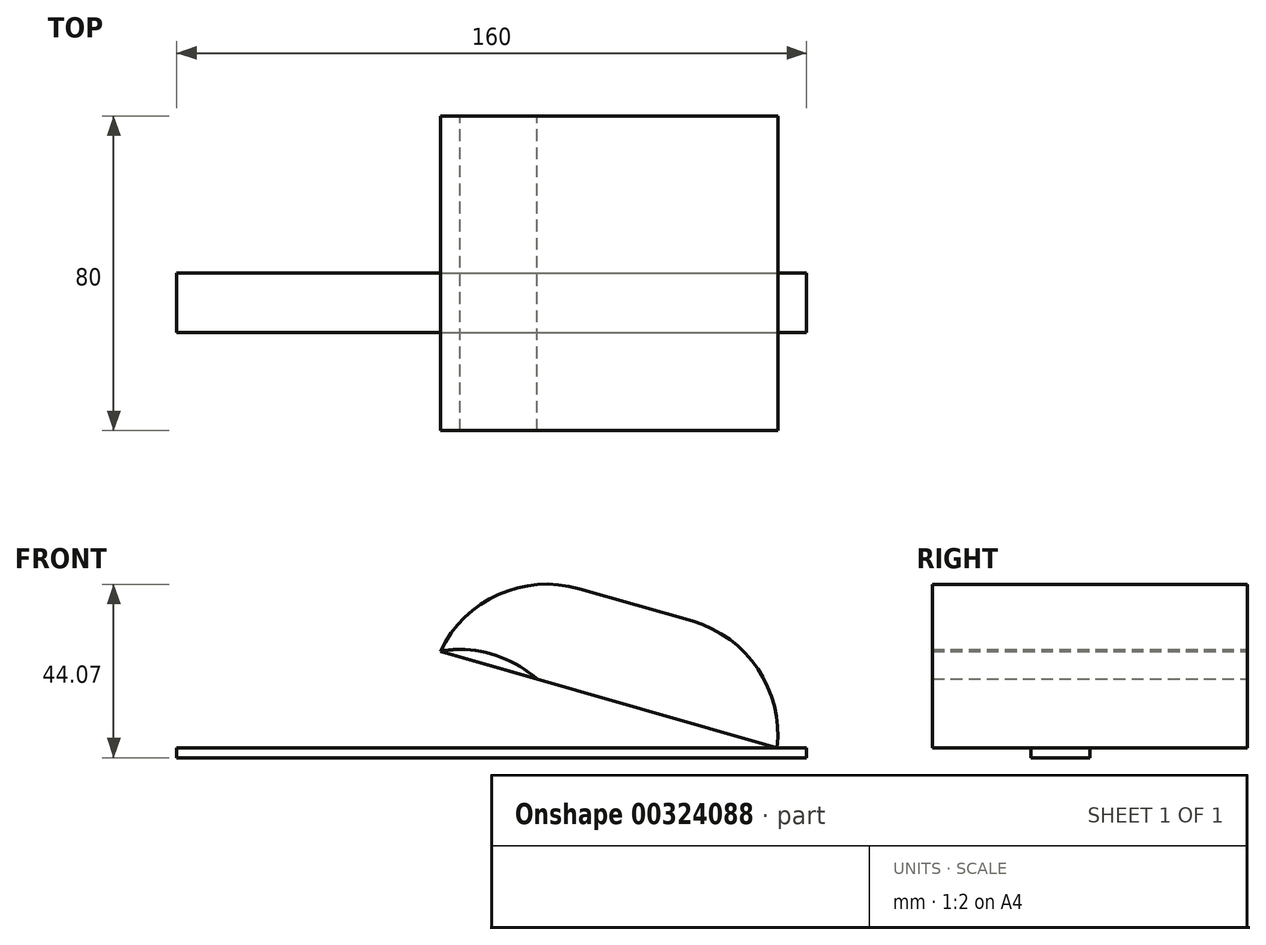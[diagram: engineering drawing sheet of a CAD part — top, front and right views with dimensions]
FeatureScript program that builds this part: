
annotation { "Feature Type Name" : "Feature", "Feature Type Description" : "" }
export const myFeature = defineFeature(function(context is Context, id is Id, definition is map)
    precondition{}
    {
        {
            var Q0;
            Q0=qCreatedBy(makeId("Front.planeOp"),FACE);
            var sketch = newSketch(context, id + "F0", { "sketchPlane" : qUnion([Q0])});
            skLineSegment(sketch, "E0.bottom", {"start": v(-80, 0) * mm, "end": v(80, 0) * mm});
            skLineSegment(sketch, "E0.top", {"start": v(-80, 2.5) * mm, "end": v(80, 2.5) * mm});
            skLineSegment(sketch, "E0.right", {"start": v(80, 0) * mm, "end": v(80, 2.5) * mm});
            skLineSegment(sketch, "E1", {"start": v(77.5, 0) * mm, "end": v(77.5, 2.5) * mm});
            skLineSegment(sketch, "E2", {"start": v(-77.5, 27.5) * mm, "end": v(11.5, 27.5) * mm});
            skLineSegment(sketch, "E3", {"start": v(11.5, 27.5) * mm, "end": v(11.5, 2.5) * mm});
            skLineSegment(sketch, "E4", {"start": v(11.5, 2.5) * mm, "end": v(-77.5, 2.5) * mm});
            skLineSegment(sketch, "E5", {"start": v(-6.16, 51.06) * mm, "end": v(79.4, 26.53) * mm});
            skLineSegment(sketch, "E6", {"start": v(79.4, 26.53) * mm, "end": v(72.5, 2.5) * mm});
            skLineSegment(sketch, "E7", {"start": v(72.5, 2.5) * mm, "end": v(-13.05, 27.03) * mm});
            skLineSegment(sketch, "E8", {"start": v(-13.05, 27.03) * mm, "end": v(-6.16, 51.06) * mm});
            skLineSegment(sketch, "E9", {"start": v(-77.5, 27.5) * mm, "end": v(-77.5, 2.5) * mm});
            skLineSegment(sketch, "E10", {"start": v(-80, 2.5) * mm, "end": v(-80, 0) * mm});
            skLineSegment(sketch, "E11.bottom", {"start": v(-80, 2.5) * mm, "end": v(-77.5, 2.5) * mm});
            skLineSegment(sketch, "E11.top", {"start": v(-80, 17.5) * mm, "end": v(-77.5, 17.5) * mm});
            skLineSegment(sketch, "E11.left", {"start": v(-80, 2.5) * mm, "end": v(-80, 17.5) * mm});
            skLineSegment(sketch, "E11.right", {"start": v(-77.5, 2.5) * mm, "end": v(-77.5, 17.5) * mm});
            skLineSegment(sketch, "E12.bottom", {"start": v(77.5, 2.5) * mm, "end": v(80, 2.5) * mm});
            skLineSegment(sketch, "E12.top", {"start": v(77.5, 17.5) * mm, "end": v(80, 17.5) * mm});
            skLineSegment(sketch, "E12.left", {"start": v(77.5, 2.5) * mm, "end": v(77.5, 17.5) * mm});
            skLineSegment(sketch, "E12.right", {"start": v(80, 2.5) * mm, "end": v(80, 17.5) * mm});
            skSolve(sketch);
        }
        {
            var Q0;
            Q0=makeQuery(id+"F0.imprint","IMPRINT",FACE,{"disambiguationData":[TD([[makeQuery(id+"F0.imprint","IMPRINT",EDGE,{"derivedFrom":sQuery(id+"F0.wireOp",EDGE,"E11.bottom")}),1.0]])]});
            var Q1;
            {var subQ0=sQuery(id+"F0.wireOp",EDGE,"E1");Q1=makeQuery(id+"F0.imprint","IMPRINT",FACE,{"disambiguationData":[TD([[makeQuery(id+"F0.imprint","IMPRINT",EDGE,{"derivedFrom":subQ0}),1.0]])]});}
            var Q2;
            {var subQ0=sQuery(id+"F0.wireOp",EDGE,"E0.right");Q2=makeQuery(id+"F0.imprint","IMPRINT",FACE,{"disambiguationData":[TD([[makeQuery(id+"F0.imprint","IMPRINT",EDGE,{"derivedFrom":subQ0}),1.0]])]});}
            var Q3;
            Q3=makeQuery(id+"F0.imprint","IMPRINT",FACE,{"disambiguationData":[TD([[makeQuery(id+"F0.imprint","IMPRINT",EDGE,{"derivedFrom":sQuery(id+"F0.wireOp",EDGE,"E12.bottom")}),1.0]])]});
            extrude(context, id + "F1", {"entities" : qUnion([Q0, Q1, Q2, Q3]), "depth" : 15 * mm, "offsetDistance" : 25 * mm});
        }
        {
            var Q0;
            {var subQ0=sQuery(id+"F0.wireOp",EDGE,"E4");Q0=makeQuery(id+"F0.imprint","IMPRINT",FACE,{"disambiguationData":[TD([[makeQuery(id+"F0.imprint","IMPRINT",EDGE,{"derivedFrom":subQ0}),-1.0]])]});}
            var Q1;
            {var subQ0=sQuery(id+"F0.wireOp",EDGE,"E3");var subQ1=sQuery(id+"F0.wireOp",EDGE,"E2");var subQ2=makeQuery(id+"F0.imprint","INTERSECT",VERTEX,{"derivedFrom":[subQ1,subQ0]});Q1=makeQuery(id+"F0.imprint","IMPRINT",FACE,{"disambiguationData":[TD([[makeQuery(id+"F0.imprint","IMPRINT",EDGE,{"disambiguationData":[TD([[subQ2,1.0]])],"derivedFrom":subQ1}),-1.0]])]});}
            extrude(context, id + "F2", {"entities" : qUnion([Q0, Q1]), "endBound" : BoundingType.SYMMETRIC, "depth" : 80 * mm, "offsetDistance" : 25 * mm});
        }
        {
            var Q0;
            Q0=makeQuery(id+"F2.opExtrude","SWEPT_EDGE",EDGE,{"disambiguationData":[OSD([sQuery(id+"F0.wireOp",EDGE,"E2"),sQuery(id+"F0.wireOp",EDGE,"E9")])]});
            var Q1;
            Q1=makeQuery(id+"F2.opExtrude","SWEPT_EDGE",EDGE,{"disambiguationData":[OSD([sQuery(id+"F0.wireOp",EDGE,"E2"),sQuery(id+"F0.wireOp",EDGE,"E3")])]});
            fillet(context, id + "F3", {"entities" : qUnion([Q0, Q1]), "radius" : 30 * mm, "tangentPropagation" : true, "allowEdgeOverflow" : false});
        }
        {
            var Q0;
            Q0=makeQuery(id+"F0.imprint","IMPRINT",FACE,{"disambiguationData":[TD([[makeQuery(id+"F0.imprint","IMPRINT",EDGE,{"derivedFrom":sQuery(id+"F0.wireOp",EDGE,"E5")}),-1.0]])]});
            var Q1;
            {var subQ0=sQuery(id+"F0.wireOp",EDGE,"E3");var subQ1=sQuery(id+"F0.wireOp",EDGE,"E2");var subQ2=makeQuery(id+"F0.imprint","INTERSECT",VERTEX,{"derivedFrom":[subQ1,subQ0]});Q1=makeQuery(id+"F0.imprint","IMPRINT",FACE,{"disambiguationData":[TD([[makeQuery(id+"F0.imprint","IMPRINT",EDGE,{"disambiguationData":[TD([[subQ2,1.0]])],"derivedFrom":subQ1}),-1.0]])]});}
            extrude(context, id + "F4", {"entities" : qUnion([Q0, Q1]), "endBound" : BoundingType.SYMMETRIC, "oppositeDirection" : true, "depth" : 80 * mm, "offsetDistance" : 25 * mm, "hasSecondDirection" : true, "secondDirectionOppositeDirection" : false, "secondDirectionDepth" : 25 * mm});
        }
        {
            var Q0;
            Q0=makeQuery(id+"F4.opExtrude","SWEPT_EDGE",EDGE,{"disambiguationData":[OSD([sQuery(id+"F0.wireOp",EDGE,"E5"),sQuery(id+"F0.wireOp",EDGE,"E8")])]});
            var Q1;
            Q1=makeQuery(id+"F4.opExtrude","SWEPT_EDGE",EDGE,{"disambiguationData":[OSD([sQuery(id+"F0.wireOp",EDGE,"E5"),sQuery(id+"F0.wireOp",EDGE,"E6")])]});
            fillet(context, id + "F5", {"entities" : qUnion([Q0, Q1]), "radius" : 30 * mm, "tangentPropagation" : true, "allowEdgeOverflow" : false});
        }
    });
